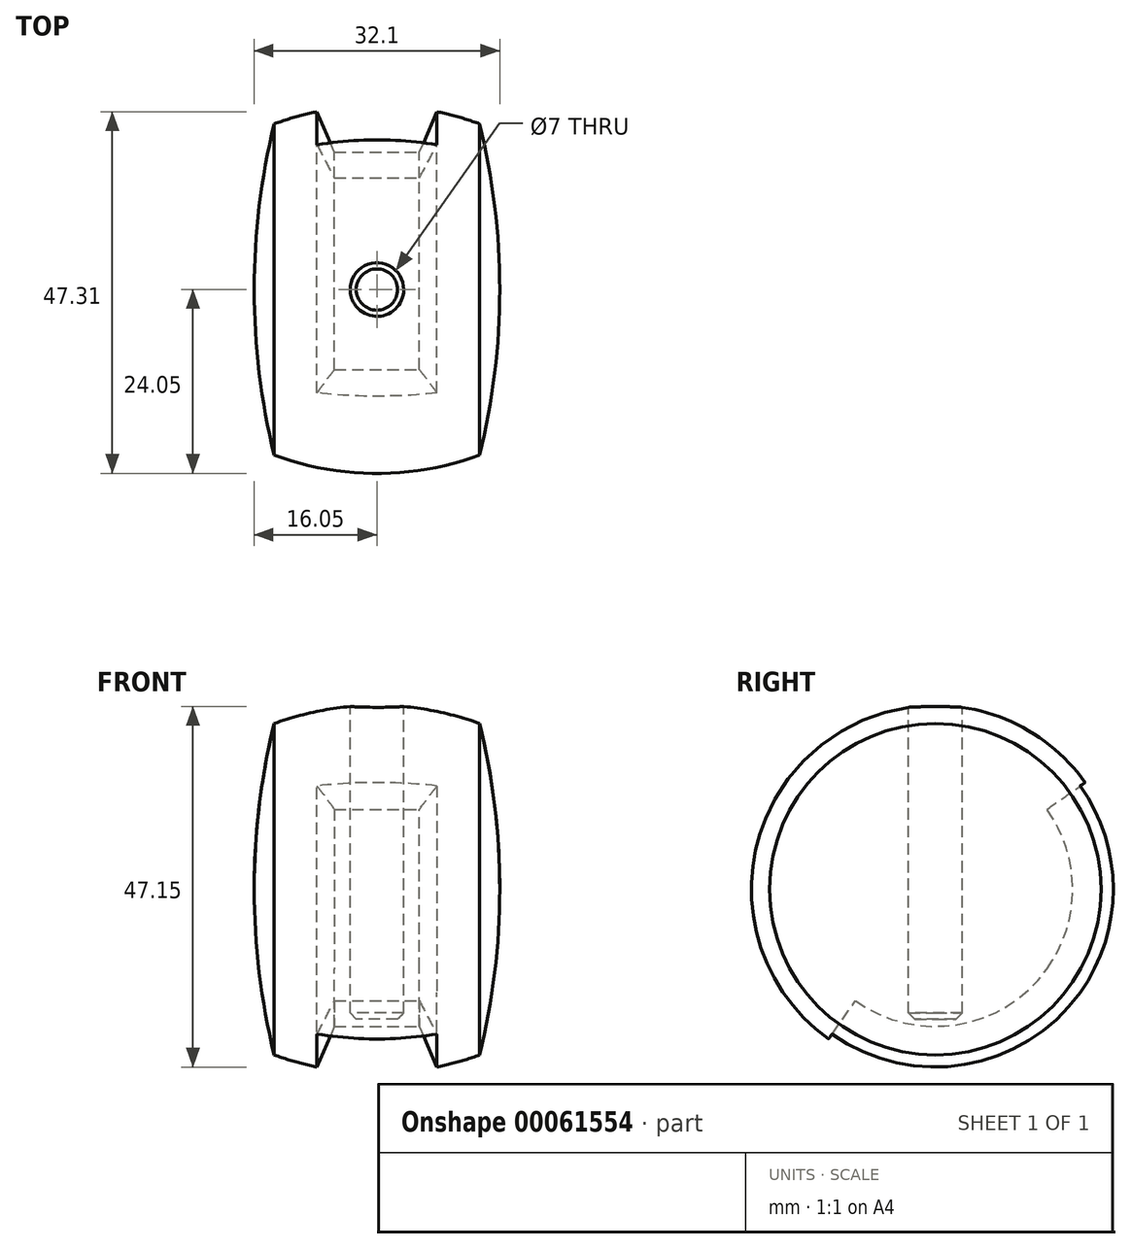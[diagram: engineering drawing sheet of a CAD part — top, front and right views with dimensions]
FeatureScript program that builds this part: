
annotation { "Feature Type Name" : "Feature", "Feature Type Description" : "" }
export const myFeature = defineFeature(function(context is Context, id is Id, definition is map)
    precondition{}
    {
        {
            var Q0;
            Q0=qCreatedBy(makeId("Top.planeOp"),FACE);
            var sketch = newSketch(context, id + "F0", { "sketchPlane" : qUnion([Q0])});
            skLineSegment(sketch, "E0.rect.bottom", {"start": v(18.5, -26.5) * mm, "end": v(-18.5, -26.5) * mm, "construction": true});
            skLineSegment(sketch, "E0.rect.top", {"start": v(18.5, 26.5) * mm, "end": v(-18.5, 26.5) * mm, "construction": true});
            skLineSegment(sketch, "E0.rect.left", {"start": v(18.5, -26.5) * mm, "end": v(18.5, 26.5) * mm, "construction": true});
            skLineSegment(sketch, "E0.rect.right", {"start": v(-18.5, -26.5) * mm, "end": v(-18.5, 26.5) * mm, "construction": true});
            skPoint(sketch, "E0.rect.middle", {"position": v(0, 0) * mm});
            skLineSegment(sketch, "E1.0", {"start": v(15.5, 23.5) * mm, "end": v(-15.5, 23.5) * mm, "construction": true});
            skLineSegment(sketch, "E1.1", {"start": v(15.5, -23.5) * mm, "end": v(15.5, 23.5) * mm, "construction": true});
            skLineSegment(sketch, "E1.2", {"start": v(15.5, -23.5) * mm, "end": v(-15.5, -23.5) * mm, "construction": true});
            skLineSegment(sketch, "E1.3", {"start": v(-15.5, -23.5) * mm, "end": v(-15.5, 23.5) * mm, "construction": true});
            skLineSegment(sketch, "E2", {"start": v(-85.97, 0) * mm, "end": v(85.97, 0) * mm, "construction": true});
            skArc(sketch, "E3", {"start": v(15.5, 23.5) * mm, "mid": v(0, 26.5) * mm, "end": v(-15.5, 23.5) * mm});
            skArc(sketch, "E4", {"start": v(-15.5, 23.5) * mm, "mid": v(-17.75, 11.85) * mm, "end": v(-18.5, 0) * mm});
            skLineSegment(sketch, "E5", {"start": v(0, 34.12) * mm, "end": v(0, -34.12) * mm, "construction": true});
            skPoint(sketch, "E5.endSnap0", {"position": v(0, -26.5) * mm});
            skArc(sketch, "E6.MirrorCS", {"start": v(15.5, 23.5) * mm, "mid": v(17.75, 11.85) * mm, "end": v(18.5, 0) * mm});
            skPoint(sketch, "E7.orphan", {"position": v(15.5, -23.5) * mm});
            skPoint(sketch, "E8.MirrorCS.end.orphan", {"position": v(-15.5, -23.5) * mm});
            skArc(sketch, "E9.0", {"start": v(-14.24, 22.38) * mm, "mid": v(-16.3, 11.28) * mm, "end": v(-17, 0) * mm});
            skArc(sketch, "E9.1", {"start": v(14.24, 22.38) * mm, "mid": v(0, 25) * mm, "end": v(-14.24, 22.38) * mm});
            skArc(sketch, "E9.2", {"start": v(14.24, 22.38) * mm, "mid": v(16.3, 11.28) * mm, "end": v(17, 0) * mm});
            skLineSegment(sketch, "E10", {"start": v(-18.5, 0) * mm, "end": v(-17, 0) * mm});
            skLineSegment(sketch, "E11", {"start": v(17, 0) * mm, "end": v(18.5, 0) * mm});
            skLineSegment(sketch, "E12", {"start": v(-8.02, 24.19) * mm, "end": v(-5.41, 18.14) * mm});
            skLineSegment(sketch, "E13", {"start": v(-5.41, 18.14) * mm, "end": v(5.41, 18.14) * mm});
            skLineSegment(sketch, "E14", {"start": v(5.41, 18.14) * mm, "end": v(8.02, 24.19) * mm});
            skSolve(sketch);
        }
        {
            var Q0;
            {var subQ0=sQuery(id+"F0.wireOp",EDGE,"E12");Q0=makeQuery(id+"F0.imprint","IMPRINT",FACE,{"disambiguationData":[TD([[makeQuery(id+"F0.imprint","IMPRINT",EDGE,{"derivedFrom":subQ0}),1.0]])]});}
            var Q1;
            Q1=sQuery(id+"F0.wireOp",EDGE,"E2");
            revolve(context, id + "F1", {"entities" : qUnion([Q0]), "axis" : qUnion([Q1]), "revolveType" : RevolveType.SYMMETRIC, "oppositeDirection" : true, "angle" : 70 * degree});
        }
        {
            var Q0;
            Q0=qCreatedBy(makeId("Front.planeOp"),FACE);
            var sketch = newSketch(context, id + "F2", { "sketchPlane" : qUnion([Q0])});
            skLineSegment(sketch, "E15.rect.bottom", {"start": v(18.5, -26.5) * mm, "end": v(-18.5, -26.5) * mm, "construction": true});
            skLineSegment(sketch, "E15.rect.top", {"start": v(18.5, 26.5) * mm, "end": v(-18.5, 26.5) * mm, "construction": true});
            skLineSegment(sketch, "E15.rect.left", {"start": v(18.5, -26.5) * mm, "end": v(18.5, 26.5) * mm, "construction": true});
            skLineSegment(sketch, "E15.rect.right", {"start": v(-18.5, -26.5) * mm, "end": v(-18.5, 26.5) * mm, "construction": true});
            skPoint(sketch, "E15.rect.middle", {"position": v(0, 0) * mm});
            skLineSegment(sketch, "E16.0", {"start": v(15.5, 23.5) * mm, "end": v(-15.5, 23.5) * mm, "construction": true});
            skLineSegment(sketch, "E16.1", {"start": v(15.5, -23.5) * mm, "end": v(15.5, 23.5) * mm, "construction": true});
            skLineSegment(sketch, "E16.2", {"start": v(15.5, -23.5) * mm, "end": v(-15.5, -23.5) * mm, "construction": true});
            skLineSegment(sketch, "E16.3", {"start": v(-15.5, -23.5) * mm, "end": v(-15.5, 23.5) * mm, "construction": true});
            skLineSegment(sketch, "E17", {"start": v(-52.75, 0) * mm, "end": v(55.66, 0) * mm, "construction": true});
            skArc(sketch, "E18", {"start": v(15.5, 23.5) * mm, "mid": v(0, 26.5) * mm, "end": v(-15.5, 23.5) * mm});
            skArc(sketch, "E19", {"start": v(-15.5, 23.5) * mm, "mid": v(-17.75, 11.85) * mm, "end": v(-18.5, 0) * mm});
            skLineSegment(sketch, "E20", {"start": v(0, 37.06) * mm, "end": v(0, -36.72) * mm, "construction": true});
            skPoint(sketch, "E20.endSnap0", {"position": v(0, -26.5) * mm});
            skArc(sketch, "E21.MirrorCS", {"start": v(15.5, 23.5) * mm, "mid": v(17.75, 11.85) * mm, "end": v(18.5, 0) * mm});
            skPoint(sketch, "E22.orphan", {"position": v(15.5, -23.5) * mm});
            skPoint(sketch, "E23.MirrorCS.center.orphan", {"position": v(0, 15.04) * mm});
            skPoint(sketch, "E23.MirrorCS.end.orphan", {"position": v(-15.5, -23.5) * mm});
            skArc(sketch, "E24.0", {"start": v(-13.65, 21.86) * mm, "mid": v(-15.63, 11) * mm, "end": v(-16.3, 0) * mm});
            skArc(sketch, "E24.1", {"start": v(13.65, 21.86) * mm, "mid": v(0, 24.3) * mm, "end": v(-13.65, 21.86) * mm});
            skArc(sketch, "E24.2", {"start": v(13.65, 21.86) * mm, "mid": v(15.63, 11) * mm, "end": v(16.3, 0) * mm});
            skLineSegment(sketch, "E25", {"start": v(16.3, 0) * mm, "end": v(18.5, 0) * mm});
            skLineSegment(sketch, "E26", {"start": v(-18.5, 0) * mm, "end": v(-16.3, 0) * mm});
            skSolve(sketch);
        }
        {
            var Q0;
            Q0=qCreatedBy(makeId("Front.planeOp"),FACE);
            var sketch = newSketch(context, id + "F3", { "sketchPlane" : qUnion([Q0])});
            skPoint(sketch, "E27.rect.middle", {"position": v(0, 0) * mm});
            skLineSegment(sketch, "E28", {"start": v(-52.75, 0) * mm, "end": v(55.66, 0) * mm, "construction": true});
            skLineSegment(sketch, "E29", {"start": v(0, 36.48) * mm, "end": v(0, -37.3) * mm, "construction": true});
            skArc(sketch, "E30.0", {"start": v(-13.82, 21.43) * mm, "mid": v(-15.72, 10.79) * mm, "end": v(-16.36, 0) * mm, "construction": true});
            skArc(sketch, "E30.1", {"start": v(13.82, 21.43) * mm, "mid": v(0, 23.92) * mm, "end": v(-13.82, 21.43) * mm, "construction": true});
            skArc(sketch, "E30.2", {"start": v(13.82, 21.43) * mm, "mid": v(15.72, 10.79) * mm, "end": v(16.36, 0) * mm, "construction": true});
            skLineSegment(sketch, "E31", {"start": v(-16.05, 0) * mm, "end": v(16.05, 0) * mm});
            skArc(sketch, "E32.0", {"start": v(-13.65, 21.86) * mm, "mid": v(-15.63, 11) * mm, "end": v(-16.3, 0) * mm, "construction": true});
            skArc(sketch, "E33.0", {"start": v(13.65, 21.86) * mm, "mid": v(0, 24.3) * mm, "end": v(-13.65, 21.86) * mm, "construction": true});
            skArc(sketch, "E34.0", {"start": v(13.65, 21.86) * mm, "mid": v(15.63, 11) * mm, "end": v(16.3, 0) * mm, "construction": true});
            skArc(sketch, "E35.0", {"start": v(-13.44, 21.67) * mm, "mid": v(-15.4, 10.91) * mm, "end": v(-16.05, 0) * mm});
            skArc(sketch, "E35.1", {"start": v(13.44, 21.67) * mm, "mid": v(0, 24.05) * mm, "end": v(-13.44, 21.67) * mm});
            skArc(sketch, "E35.2", {"start": v(13.44, 21.67) * mm, "mid": v(15.4, 10.91) * mm, "end": v(16.05, 0) * mm});
            skSolve(sketch);
        }
        {
            var Q0;
            Q0=qSketchRegion(id+"F3",true);
            var Q1;
            Q1=sQuery(id+"F3.wireOp",EDGE,"E28");
            revolve(context, id + "F4", {"entities" : qUnion([Q0]), "axis" : qUnion([Q1]), "revolveType" : RevolveType.FULL});
        }
        {
            var Q0;
            Q0=qCreatedBy(makeId("Top.planeOp"),FACE);
            var sketch = newSketch(context, id + "F5", { "sketchPlane" : qUnion([Q0])});
            skCircle(sketch, "E36", {"center": v(0, 0) * mm, "radius": 3.5 * mm});
            skSolve(sketch);
        }
        {
            var Q0;
            Q0=qSketchRegion(id+"F5",true);
            extrude(context, id + "F6", {"entities" : qUnion([Q0]), "operationType" : NewBodyOperationType.REMOVE, "oppositeDirection" : true, "depth" : 17 * mm, "hasSecondDirection" : true, "secondDirectionBound" : BoundingType.THROUGH_ALL, "secondDirectionOppositeDirection" : false, "secondDirectionDepth" : 15 * mm});
        }
        {
            var Q0;
            Q0=makeQuery(id+"F1.opRevolve","SWEPT_BODY",BODY,{"disambiguationData":[OSD([sQuery(id+"F0.wireOp",EDGE,"E9.1"),sQuery(id+"F0.wireOp",EDGE,"E12"),sQuery(id+"F0.wireOp",EDGE,"E13"),sQuery(id+"F0.wireOp",EDGE,"E14")])]});
            var Q1;
            Q1=makeQuery(id+"F4.opRevolve","SWEPT_BODY",BODY,{"disambiguationData":[OSD([sQuery(id+"F3.wireOp",EDGE,"E30.0"),sQuery(id+"F3.wireOp",EDGE,"E30.1"),sQuery(id+"F3.wireOp",EDGE,"E30.2"),sQuery(id+"F3.wireOp",EDGE,"E31")])]});
            booleanBodies(context, id + "F7", {"operationType" : BooleanOperationType.SUBTRACTION, "tools" : qUnion([Q0]), "targets" : qUnion([Q1]), "offset" : true, "offsetAll" : true, "offsetDistance" : 0.2 * mm});
        }
        {
            var Q0;
            Q0=makeQuery(id+"F7.tempBoolean.opBoolean","COPY",FACE,{"derivedFrom":makeQuery(id+"F7.offsetTempBody.opPattern","COPY",FACE,{"derivedFrom":makeQuery(id+"F1.opRevolve","CAP_FACE",FACE,{"disambiguationData":[OSD([sQuery(id+"F0.wireOp",EDGE,"E9.1"),sQuery(id+"F0.wireOp",EDGE,"E12"),sQuery(id+"F0.wireOp",EDGE,"E13"),sQuery(id+"F0.wireOp",EDGE,"E14")])],"isStart":false}),"instanceName":"1"})});
            var Q1;
            Q1=sQuery(id+"F0.wireOp",EDGE,"E2");
            revolve(context, id + "F8", {"operationType" : NewBodyOperationType.REMOVE, "entities" : qUnion([Q0]), "axis" : qUnion([Q1]), "revolveType" : RevolveType.ONE_DIRECTION, "oppositeDirection" : true, "angle" : 90 * degree});
        }
        {
            var Q0;
            Q0=makeQuery(id+"F6.boolean.opBoolean","COPY",EDGE,{"derivedFrom":makeQuery(id+"F6.opExtrude","CAP_EDGE",EDGE,{"disambiguationData":[OSD([sQuery(id+"F5.wireOp",EDGE,"E36")])],"isStart":false})});
            chamfer(context, id + "F9", {"entities" : qUnion([Q0]), "width" : 0.8 * mm, "tangentPropagation" : true});
        }
    });
